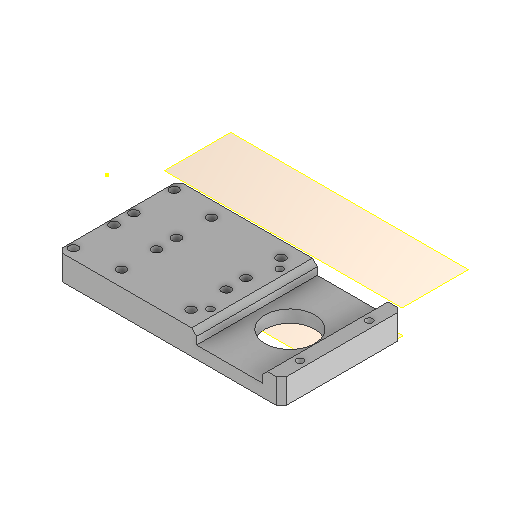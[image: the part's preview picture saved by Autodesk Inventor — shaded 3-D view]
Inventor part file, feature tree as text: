
AUTODESK INVENTOR PART (.ipt)
format: ipt  version: 2024.1 (Build 281209000, 209)  size: 217,088 bytes
history: native  units: mm
features: sketch x5, other x5, reference x4, plane x2, extrude x2, hole x2, projected_geometry x2, chamfer x1
ambient origin geometry x8: Origin, YZ Plane, XZ Plane, XY Plane, X Axis, Y Axis, Z Axis, Center Point
bodies: Body1 (feature_tree)
feature tree (23):
  plane  "Arbeitsebene1"
  plane  "Arbeitsebene2"
  extrude  "Extrusion6"  Depth=10.0mm
  extrude  "Extrusion7"  Depth=5.0mm
  chamfer  "Fasen2"  Distance=5.0mm
  hole  "Bohrung3"  [1 undecoded]
  sketch  "Skizze11"  dims[d44=3.6mm d45=6.0mm d46=4.0mm d47=2.0mm d48=90.0deg d49=15.0mm d50=20.594885mm d51=36.0mm]
  hole  "Bohrung4"  [1 undecoded]
  sketch  "Skizze8"  dims[d34=10.0mm d35=0.0mm d36=20.0mm]
  reference  "Referenz12"
  reference  "Referenz13"
  reference  "Referenz14"
  sketch  "Skizze9"  dims[d37=0.5mm d38=5.0mm d39=5.0mm d40=0.0mm]
  reference  "Referenz15"
  sketch  "Skizze10"  dims[d41=2.0mm d42=2.0mm d43=45.0deg]
  projected_geometry  "Projizierte Kontur7"
  sketch  "Skizze12"  dims[d52=28.0mm d53=2.8mm d54=6.0mm d55=4.0mm d56=2.0mm d57=90.0deg d58=15.0mm d59=20.594885mm d21=0.5mm d22=0.872665mm d23=0.5mm d24=0.872665mm d27=0.5mm d28=0.872665mm d29=0.5mm d30=0.872665mm]
  projected_geometry  "Projizierte Kontur8"
  other  "Assembly_Planktoscope_Uc2version_wormdrive_V3.iam"
  other  "60_Planktoscope_Base_half_wormdrive_1:1"
  other  "60_Planktoscope_Base_half_wormdrive_1_MIR:1"
  other  "00_Microscope_Slide:1"
  other  "60_Planktoscope_Base_half1_MIR:1"
note: 2 required parameter values undecoded (feature->parameter linkage not recoverable at this tier; creation-order binding heuristic only, values carry confidence <= 0.55)
